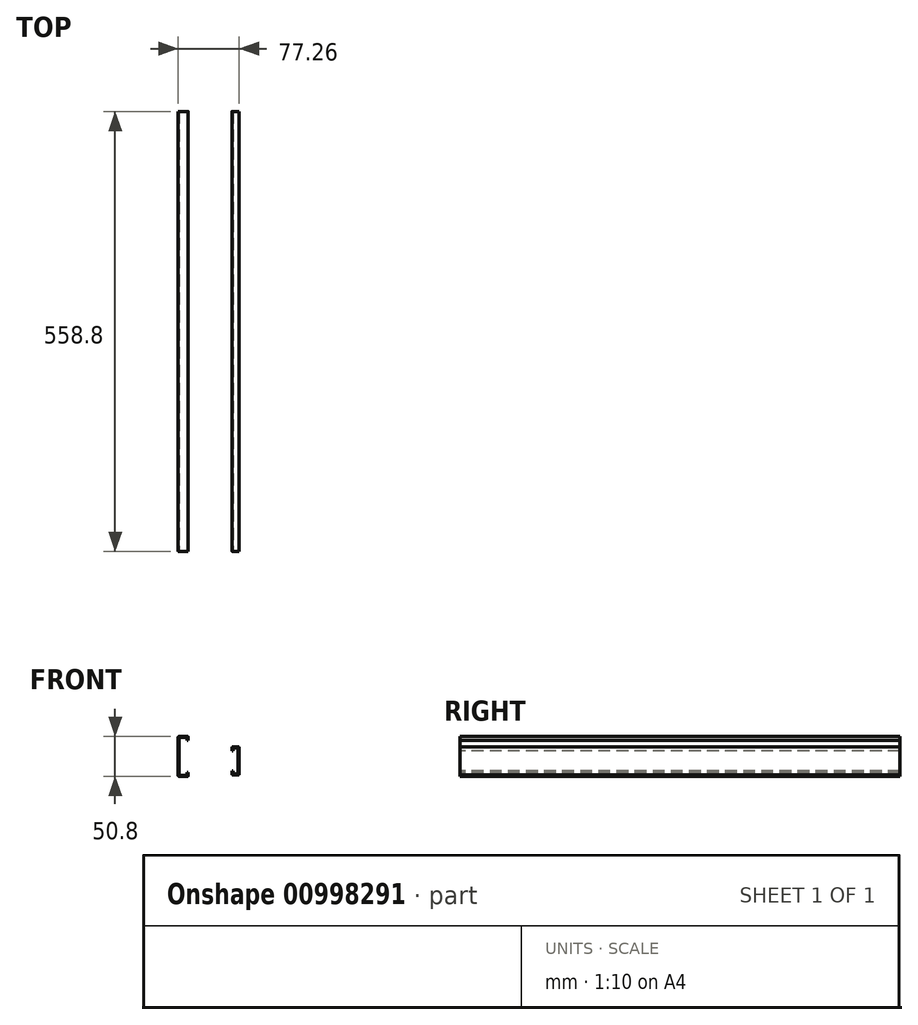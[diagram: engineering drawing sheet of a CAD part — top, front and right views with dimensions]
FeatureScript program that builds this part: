
annotation { "Feature Type Name" : "Feature", "Feature Type Description" : "" }
export const myFeature = defineFeature(function(context is Context, id is Id, definition is map)
    precondition{}
    {
        {
            var Q0;
            Q0=qCreatedBy(makeId("Front.planeOp"),FACE);
            var sketch = newSketch(context, id + "F0", { "sketchPlane" : qUnion([Q0])});
            skLineSegment(sketch, "E0.bottom", {"start": v(-11.94, 50.8) * mm, "end": v(-0.76, 50.8) * mm});
            skLineSegment(sketch, "E0.top", {"start": v(-11.94, 0) * mm, "end": v(-0.76, 0) * mm});
            skLineSegment(sketch, "E0.left", {"start": v(-12.7, 50.04) * mm, "end": v(-12.7, 0.76) * mm});
            skPoint(sketch, "E1.visualSharp", {"position": v(-12.7, 50.8) * mm});
            skArc(sketch, "E1.filletArc", {"start": v(-11.94, 50.8) * mm, "mid": v(-12.48, 50.58) * mm, "end": v(-12.7, 50.04) * mm});
            skPoint(sketch, "E2.visualSharp", {"position": v(0, 50.8) * mm});
            skArc(sketch, "E2.filletArc", {"start": v(0, 50.04) * mm, "mid": v(-0.22, 50.58) * mm, "end": v(-0.76, 50.8) * mm});
            skPoint(sketch, "E3.visualSharp", {"position": v(-12.7, 0) * mm});
            skArc(sketch, "E3.filletArc", {"start": v(-12.7, 0.76) * mm, "mid": v(-12.48, 0.22) * mm, "end": v(-11.94, 0) * mm});
            skPoint(sketch, "E4.visualSharp", {"position": v(0, 0) * mm});
            skArc(sketch, "E4.filletArc", {"start": v(-0.76, 0) * mm, "mid": v(-0.22, 0.22) * mm, "end": v(0, 0.76) * mm});
            skLineSegment(sketch, "E5", {"start": v(0, 50.04) * mm, "end": v(0, 45.72) * mm});
            skLineSegment(sketch, "E6", {"start": v(0, 0.76) * mm, "end": v(0, 5.08) * mm});
            skLineSegment(sketch, "E7", {"start": v(0, 45.72) * mm, "end": v(-1.27, 45.72) * mm});
            skLineSegment(sketch, "E8", {"start": v(-1.27, 45.72) * mm, "end": v(-1.27, 49.02) * mm});
            skLineSegment(sketch, "E9", {"start": v(-1.78, 49.53) * mm, "end": v(-10.92, 49.53) * mm});
            skLineSegment(sketch, "E10", {"start": v(-11.43, 49.02) * mm, "end": v(-11.43, 1.78) * mm});
            skLineSegment(sketch, "E11", {"start": v(-10.92, 1.27) * mm, "end": v(-1.78, 1.27) * mm});
            skLineSegment(sketch, "E12", {"start": v(-1.27, 1.78) * mm, "end": v(-1.27, 5.08) * mm});
            skLineSegment(sketch, "E13", {"start": v(-1.27, 5.08) * mm, "end": v(0, 5.08) * mm});
            skPoint(sketch, "E14.visualSharp", {"position": v(-1.27, 49.53) * mm});
            skArc(sketch, "E14.filletArc", {"start": v(-1.27, 49.02) * mm, "mid": v(-1.42, 49.38) * mm, "end": v(-1.78, 49.53) * mm});
            skPoint(sketch, "E15.visualSharp", {"position": v(-11.43, 49.53) * mm});
            skArc(sketch, "E15.filletArc", {"start": v(-10.92, 49.53) * mm, "mid": v(-11.28, 49.38) * mm, "end": v(-11.43, 49.02) * mm});
            skPoint(sketch, "E16.visualSharp", {"position": v(-11.43, 1.27) * mm});
            skArc(sketch, "E16.filletArc", {"start": v(-11.43, 1.78) * mm, "mid": v(-11.28, 1.42) * mm, "end": v(-10.92, 1.27) * mm});
            skPoint(sketch, "E17.visualSharp", {"position": v(-1.27, 1.27) * mm});
            skArc(sketch, "E17.filletArc", {"start": v(-1.78, 1.27) * mm, "mid": v(-1.42, 1.42) * mm, "end": v(-1.27, 1.78) * mm});
            skSolve(sketch);
        }
        {
            var Q0;
            Q0 = qSketchRegion(id + "F0", true);
            extrude(context, id + "F1", {"entities" : qUnion([Q0]), "oppositeDirection" : true, "depth" : 558.8 * mm, "offsetDistance" : 25.4 * mm});
        }
        {
            var Q0;
            Q0=qCreatedBy(makeId("Front.planeOp"),FACE);
            var sketch = newSketch(context, id + "F2", { "sketchPlane" : qUnion([Q0])});
            skLineSegment(sketch, "E18", {"start": v(55.44, 32.24) * mm, "end": v(55.44, 36.55) * mm});
            skLineSegment(sketch, "E19", {"start": v(56.2, 37.32) * mm, "end": v(63.8, 37.32) * mm});
            skLineSegment(sketch, "E20", {"start": v(64.56, 36.55) * mm, "end": v(64.56, 2.76) * mm});
            skLineSegment(sketch, "E21", {"start": v(63.8, 2) * mm, "end": v(56.2, 2) * mm});
            skLineSegment(sketch, "E22", {"start": v(55.44, 2.76) * mm, "end": v(55.44, 7.07) * mm});
            skLineSegment(sketch, "E23", {"start": v(55.44, 7.07) * mm, "end": v(56.7, 7.07) * mm});
            skLineSegment(sketch, "E24", {"start": v(56.7, 7.07) * mm, "end": v(56.7, 3.77) * mm});
            skLineSegment(sketch, "E25", {"start": v(57.21, 3.26) * mm, "end": v(62.79, 3.26) * mm});
            skLineSegment(sketch, "E26", {"start": v(63.3, 3.77) * mm, "end": v(63.3, 35.54) * mm});
            skLineSegment(sketch, "E27", {"start": v(62.79, 36.05) * mm, "end": v(57.21, 36.05) * mm});
            skLineSegment(sketch, "E28", {"start": v(56.7, 35.54) * mm, "end": v(56.7, 32.24) * mm});
            skLineSegment(sketch, "E29", {"start": v(56.7, 32.24) * mm, "end": v(55.44, 32.24) * mm});
            skPoint(sketch, "E30.visualSharp", {"position": v(55.44, 37.32) * mm});
            skArc(sketch, "E30.filletArc", {"start": v(56.2, 37.32) * mm, "mid": v(55.66, 37.1) * mm, "end": v(55.44, 36.55) * mm});
            skPoint(sketch, "E31.visualSharp", {"position": v(64.56, 37.32) * mm});
            skArc(sketch, "E31.filletArc", {"start": v(64.56, 36.55) * mm, "mid": v(64.34, 37.1) * mm, "end": v(63.8, 37.32) * mm});
            skPoint(sketch, "E32.visualSharp", {"position": v(64.56, 2) * mm});
            skArc(sketch, "E32.filletArc", {"start": v(63.8, 2) * mm, "mid": v(64.34, 2.22) * mm, "end": v(64.56, 2.76) * mm});
            skPoint(sketch, "E33.visualSharp", {"position": v(55.44, 2) * mm});
            skArc(sketch, "E33.filletArc", {"start": v(55.44, 2.76) * mm, "mid": v(55.66, 2.22) * mm, "end": v(56.2, 2) * mm});
            skPoint(sketch, "E34.visualSharp", {"position": v(56.7, 3.26) * mm});
            skArc(sketch, "E34.filletArc", {"start": v(56.7, 3.77) * mm, "mid": v(56.85, 3.41) * mm, "end": v(57.21, 3.26) * mm});
            skPoint(sketch, "E35.visualSharp", {"position": v(63.3, 3.26) * mm});
            skArc(sketch, "E35.filletArc", {"start": v(62.79, 3.26) * mm, "mid": v(63.14, 3.41) * mm, "end": v(63.3, 3.77) * mm});
            skPoint(sketch, "E36.visualSharp", {"position": v(63.3, 36.05) * mm});
            skArc(sketch, "E36.filletArc", {"start": v(63.3, 35.54) * mm, "mid": v(63.14, 35.9) * mm, "end": v(62.79, 36.05) * mm});
            skPoint(sketch, "E37.visualSharp", {"position": v(56.7, 36.05) * mm});
            skArc(sketch, "E37.filletArc", {"start": v(57.21, 36.05) * mm, "mid": v(56.85, 35.9) * mm, "end": v(56.7, 35.54) * mm});
            skSolve(sketch);
        }
        {
            var Q0;
            Q0 = qSketchRegion(id + "F2", true);
            var Q1;
            Q1=makeQuery(id+"F1.opExtrude","CAP_VERTEX",VERTEX,{"disambiguationData":[OSD([sQuery(id+"F0.wireOp",EDGE,"E2.filletArc"),sQuery(id+"F0.wireOp",EDGE,"E5")])],"isStart":false});
            extrude(context, id + "F3", {"entities" : qUnion([Q0]), "endBound" : BoundingType.UP_TO_VERTEX, "oppositeDirection" : true, "depth" : 25.4 * mm, "endBoundEntityVertex" : qUnion([Q1]), "offsetDistance" : 25.4 * mm});
        }
    });
